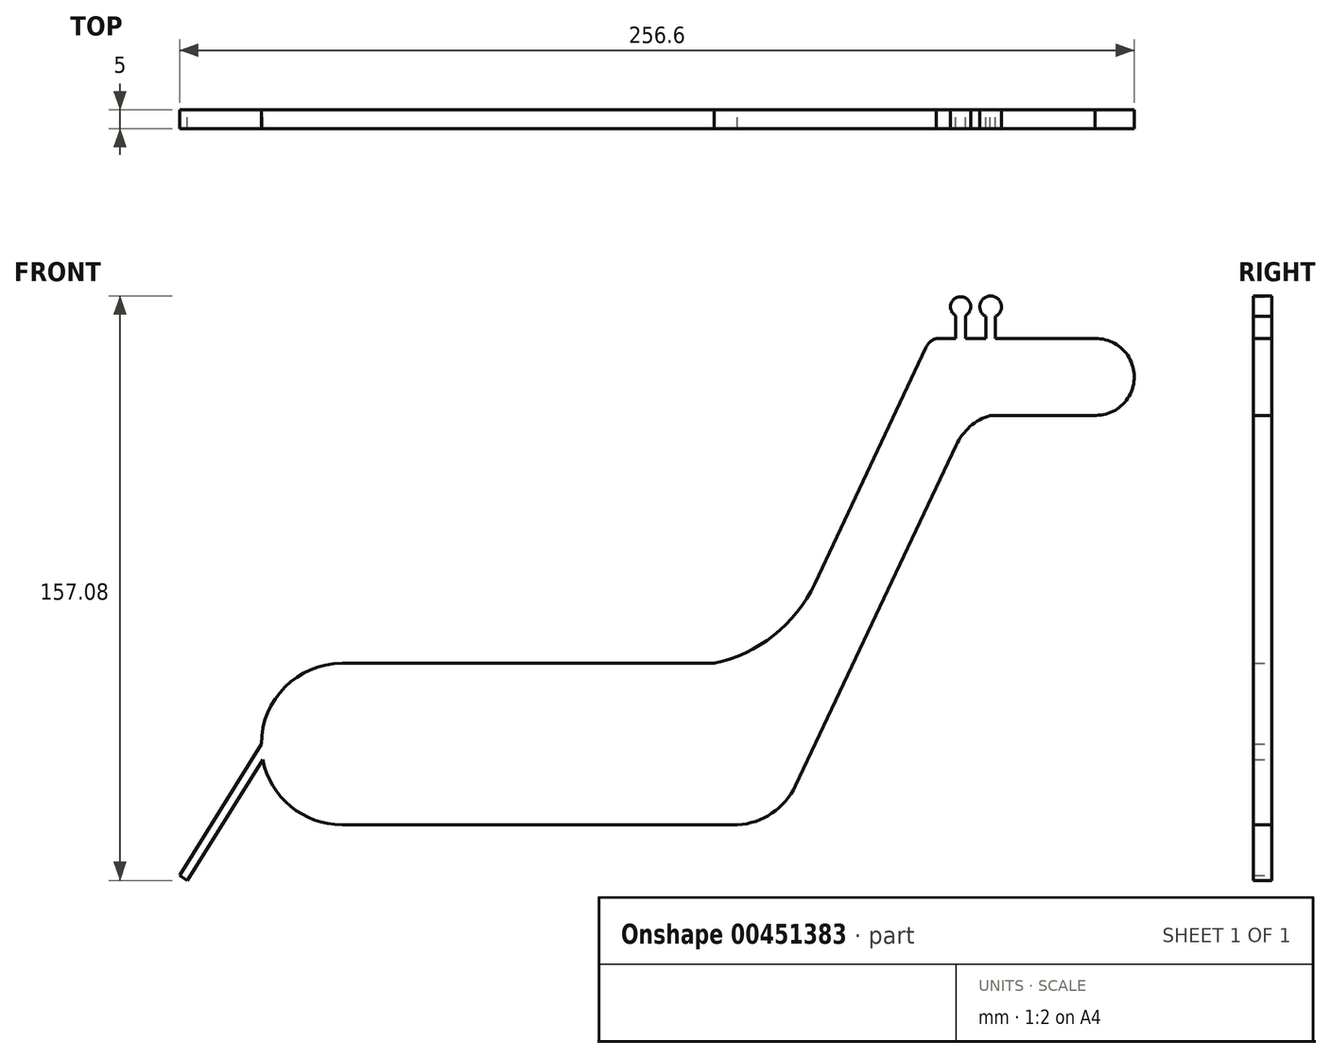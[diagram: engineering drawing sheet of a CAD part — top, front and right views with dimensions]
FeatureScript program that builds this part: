
annotation { "Feature Type Name" : "Feature", "Feature Type Description" : "" }
export const myFeature = defineFeature(function(context is Context, id is Id, definition is map)
    precondition{}
    {
        {
            var Q0;
            Q0=qCreatedBy(makeId("Front.planeOp"),FACE);
            var sketch = newSketch(context, id + "F0", { "sketchPlane" : qUnion([Q0])});
            skLineSegment(sketch, "E0.bottom", {"start": v(0, 0) * mm, "end": v(106.27, 0) * mm});
            skLineSegment(sketch, "E0.top", {"start": v(0, 43.39) * mm, "end": v(100, 43.39) * mm});
            skArc(sketch, "E1", {"start": v(0, 43.39) * mm, "mid": v(-15.34, 37.03) * mm, "end": v(-21.7, 21.7) * mm});
            skPoint(sketch, "E2.end.orphan", {"position": v(-34.92, 0) * mm});
            skPoint(sketch, "E2.start.orphan", {"position": v(-21.7, 21.7) * mm});
            skLineSegment(sketch, "E3", {"start": v(-21.7, 21.7) * mm, "end": v(-43.68, -13.62) * mm});
            skLineSegment(sketch, "E4", {"start": v(-43.68, -13.62) * mm, "end": v(-41.54, -14.95) * mm});
            skLineSegment(sketch, "E5", {"start": v(-41.54, -14.95) * mm, "end": v(-21.3, 17.55) * mm});
            skArc(sketch, "E6.trimOffspring", {"start": v(-21.3, 17.55) * mm, "mid": v(-13.8, 4.95) * mm, "end": v(0, 0) * mm});
            skLineSegment(sketch, "E7", {"start": v(121.9, 10.56) * mm, "end": v(165.01, 102.05) * mm});
            skLineSegment(sketch, "E8", {"start": v(127.01, 64.79) * mm, "end": v(156.94, 128.3) * mm});
            skLineSegment(sketch, "E9", {"start": v(159.65, 130.7) * mm, "end": v(164.93, 130.7) * mm});
            skLineSegment(sketch, "E10.left", {"start": v(167.57, 130.7) * mm, "end": v(167.57, 136.85) * mm});
            skLineSegment(sketch, "E10.right", {"start": v(164.93, 130.7) * mm, "end": v(164.93, 136.85) * mm});
            skLineSegment(sketch, "E11.left", {"start": v(175.64, 130.7) * mm, "end": v(175.64, 136.62) * mm});
            skLineSegment(sketch, "E11.right", {"start": v(173, 130.7) * mm, "end": v(173, 136.62) * mm});
            skArc(sketch, "E12", {"start": v(167.57, 136.85) * mm, "mid": v(166.25, 141.93) * mm, "end": v(164.93, 136.85) * mm});
            skArc(sketch, "E13", {"start": v(175.64, 136.62) * mm, "mid": v(174.32, 142.13) * mm, "end": v(173, 136.62) * mm});
            skPoint(sketch, "E14.orphan", {"position": v(164.93, 139.22) * mm});
            skPoint(sketch, "E15.orphan", {"position": v(167.57, 139.22) * mm});
            skPoint(sketch, "E16.orphan", {"position": v(173, 139.22) * mm});
            skPoint(sketch, "E17.orphan", {"position": v(175.64, 139.22) * mm});
            skLineSegment(sketch, "E18.trimOffspring", {"start": v(167.57, 130.7) * mm, "end": v(173, 130.7) * mm});
            skArc(sketch, "E19", {"start": v(100, 43.39) * mm, "mid": v(116.02, 50.92) * mm, "end": v(127.01, 64.79) * mm});
            skArc(sketch, "E20", {"start": v(106.27, 0) * mm, "mid": v(115.54, 3.13) * mm, "end": v(121.9, 10.56) * mm});
            skLineSegment(sketch, "E21", {"start": v(175.64, 130.7) * mm, "end": v(202.44, 130.7) * mm});
            skLineSegment(sketch, "E22", {"start": v(174.24, 110.05) * mm, "end": v(202.6, 110.05) * mm});
            skArc(sketch, "E23", {"start": v(202.6, 110.05) * mm, "mid": v(212.92, 120.45) * mm, "end": v(202.44, 130.7) * mm});
            skArc(sketch, "E24", {"start": v(174.24, 110.05) * mm, "mid": v(168.78, 107.02) * mm, "end": v(165.01, 102.05) * mm});
            skArc(sketch, "E25", {"start": v(159.65, 130.7) * mm, "mid": v(158.05, 129.77) * mm, "end": v(156.94, 128.3) * mm});
            skSolve(sketch);
        }
        {
            var Q0;
            Q0=makeQuery(id+"F0.imprint","IMPRINT",FACE,{"disambiguationData":[TD([[makeQuery(id+"F0.imprint","IMPRINT",EDGE,{"derivedFrom":sQuery(id+"F0.wireOp",EDGE,"E0.bottom")}),1.0]])]});
            extrude(context, id + "F1", {"entities" : qUnion([Q0]), "depth" : 5 * mm});
        }
    });
